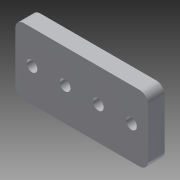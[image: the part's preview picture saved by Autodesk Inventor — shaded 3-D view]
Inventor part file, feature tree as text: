
AUTODESK INVENTOR PART (.ipt)
format: ipt  version: 2014 SP1 (Build 180222100, 222)  size: 99,840 bytes
history: native  units: in
note: dims shown in document units (in); Inventor stores cm internally (conversion verified against a paired STEP export)
features: extrude x1, sketch x1
ambient origin geometry x8: Origin, YZ Plane, XZ Plane, XY Plane, X Axis, Y Axis, Z Axis, Center Point
bodies: Solid1 (feature_tree)
feature tree (2):
  extrude  "Extrusion1"  Depth=1.0in
  sketch  "Sketch1"  dims[d0=2.0in d1=1.0in d2=0.163in d3=0.5in d4=0.25in d5=0.7874in d7=1.0in d8=0.3937in d10=1.0in d21=0.125in d22=0.25in d23=0.0in d25=0.163in d26=0.5in d27=0.5in d28=0.7874in d30=1.0in d31=0.3937in d33=1.0in]
